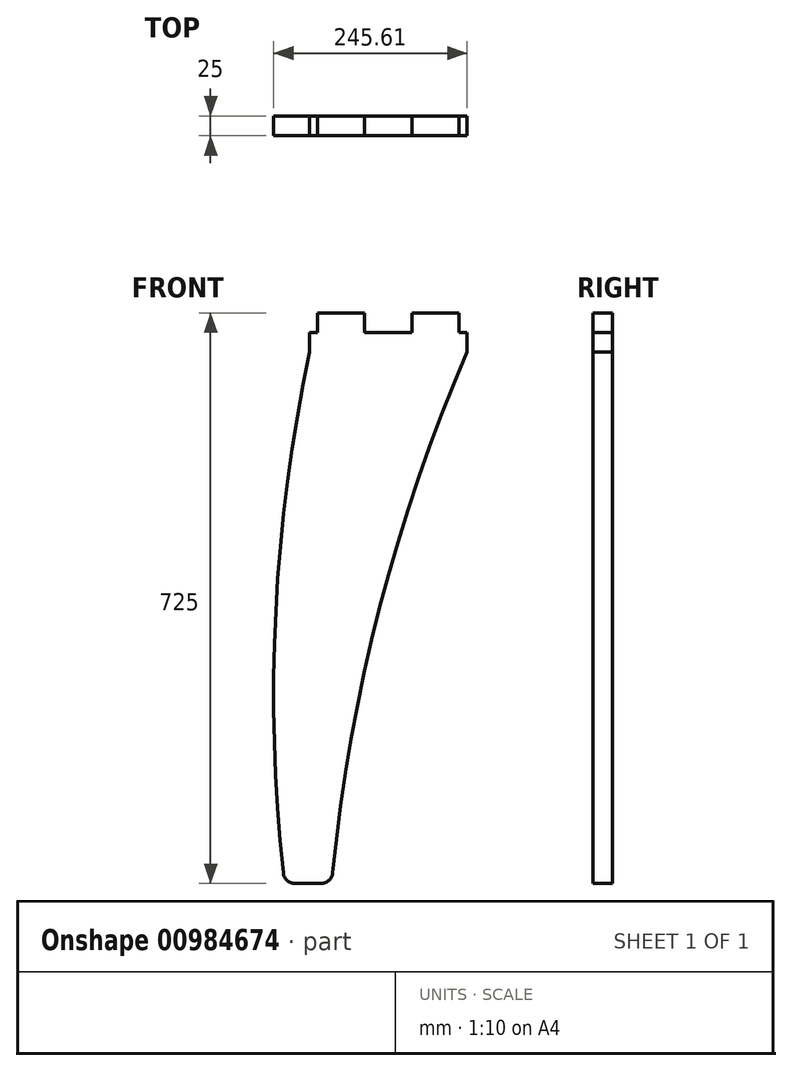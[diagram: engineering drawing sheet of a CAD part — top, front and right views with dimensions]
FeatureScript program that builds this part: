
annotation { "Feature Type Name" : "Feature", "Feature Type Description" : "" }
export const myFeature = defineFeature(function(context is Context, id is Id, definition is map)
    precondition{}
    {
        {
            var Q0;
            Q0=qCreatedBy(makeId("Front.planeOp"),FACE);
            var sketch = newSketch(context, id + "F0", { "sketchPlane" : qUnion([Q0])});
            skLineSegment(sketch, "E0", {"start": v(-396.86, 0) * mm, "end": v(405.41, 0) * mm, "construction": true});
            skLineSegment(sketch, "E1", {"start": v(0, 0) * mm, "end": v(-101.9, -725) * mm, "construction": true});
            skLineSegment(sketch, "E2", {"start": v(0, 177.04) * mm, "end": v(0, -584.61) * mm, "construction": true});
            skLineSegment(sketch, "E3", {"start": v(-811.66, -725) * mm, "end": v(607.88, -725) * mm, "construction": true});
            skLineSegment(sketch, "E4", {"start": v(-30, 0) * mm, "end": v(-30, -25) * mm});
            skLineSegment(sketch, "E5", {"start": v(30, -25) * mm, "end": v(30, 0) * mm});
            skLineSegment(sketch, "E6", {"start": v(30, 0) * mm, "end": v(90, 0) * mm});
            skLineSegment(sketch, "E7", {"start": v(90, 0) * mm, "end": v(90, -25) * mm});
            skLineSegment(sketch, "E8", {"start": v(-30, 0) * mm, "end": v(-90, 0) * mm});
            skLineSegment(sketch, "E9", {"start": v(-90, 0) * mm, "end": v(-90, -25) * mm});
            skLineSegment(sketch, "E10", {"start": v(-131.9, -176.46) * mm, "end": v(-131.9, -725) * mm, "construction": true});
            skLineSegment(sketch, "E11", {"start": v(-101.9, -725) * mm, "end": v(-101.9, -668.68) * mm, "construction": true});
            skLineSegment(sketch, "E12", {"start": v(-71.9, -725) * mm, "end": v(-71.9, -750.6) * mm, "construction": true});
            skArc(sketch, "E13", {"start": v(-100, -50) * mm, "mid": v(-143.27, -386.2) * mm, "end": v(-131.9, -725) * mm});
            skArc(sketch, "E14", {"start": v(100, -50.01) * mm, "mid": v(-12.66, -380.7) * mm, "end": v(-71.9, -725) * mm});
            skLineSegment(sketch, "E15", {"start": v(-71.9, -725) * mm, "end": v(-131.9, -725) * mm});
            skLineSegment(sketch, "E16", {"start": v(-100, -50) * mm, "end": v(-100, -25) * mm});
            skLineSegment(sketch, "E17", {"start": v(-100, -25) * mm, "end": v(-90, -25) * mm});
            skPoint(sketch, "E17.endSnap0", {"position": v(90, -25) * mm});
            skLineSegment(sketch, "E18", {"start": v(100, -25) * mm, "end": v(100, -50.01) * mm});
            skLineSegment(sketch, "E19.trimOffspring", {"start": v(90, -25) * mm, "end": v(100, -25) * mm});
            skLineSegment(sketch, "E20.trimOffspring", {"start": v(-30, -25) * mm, "end": v(30, -25) * mm});
            skPoint(sketch, "E21.start.orphan", {"position": v(90, -50) * mm});
            skSolve(sketch);
        }
        {
            var Q0;
            Q0 = qSketchRegion(id + "F0", true);
            extrude(context, id + "F1", {"entities" : qUnion([Q0]), "depth" : 25 * mm, "offsetDistance" : 25 * mm});
        }
        {
            var Q0;
            Q0=makeQuery(id+"F1.opExtrude","SWEPT_EDGE",EDGE,{"disambiguationData":[OSD([sQuery(id+"F0.wireOp",EDGE,"E14"),sQuery(id+"F0.wireOp",EDGE,"E15")])]});
            var Q1;
            Q1=makeQuery(id+"F1.opExtrude","SWEPT_EDGE",EDGE,{"disambiguationData":[OSD([sQuery(id+"F0.wireOp",EDGE,"E13"),sQuery(id+"F0.wireOp",EDGE,"E15")])]});
            fillet(context, id + "F2", {"entities" : qUnion([Q0, Q1]), "radius" : 15 * mm, "tangentPropagation" : true, "allowEdgeOverflow" : false});
        }
    });
